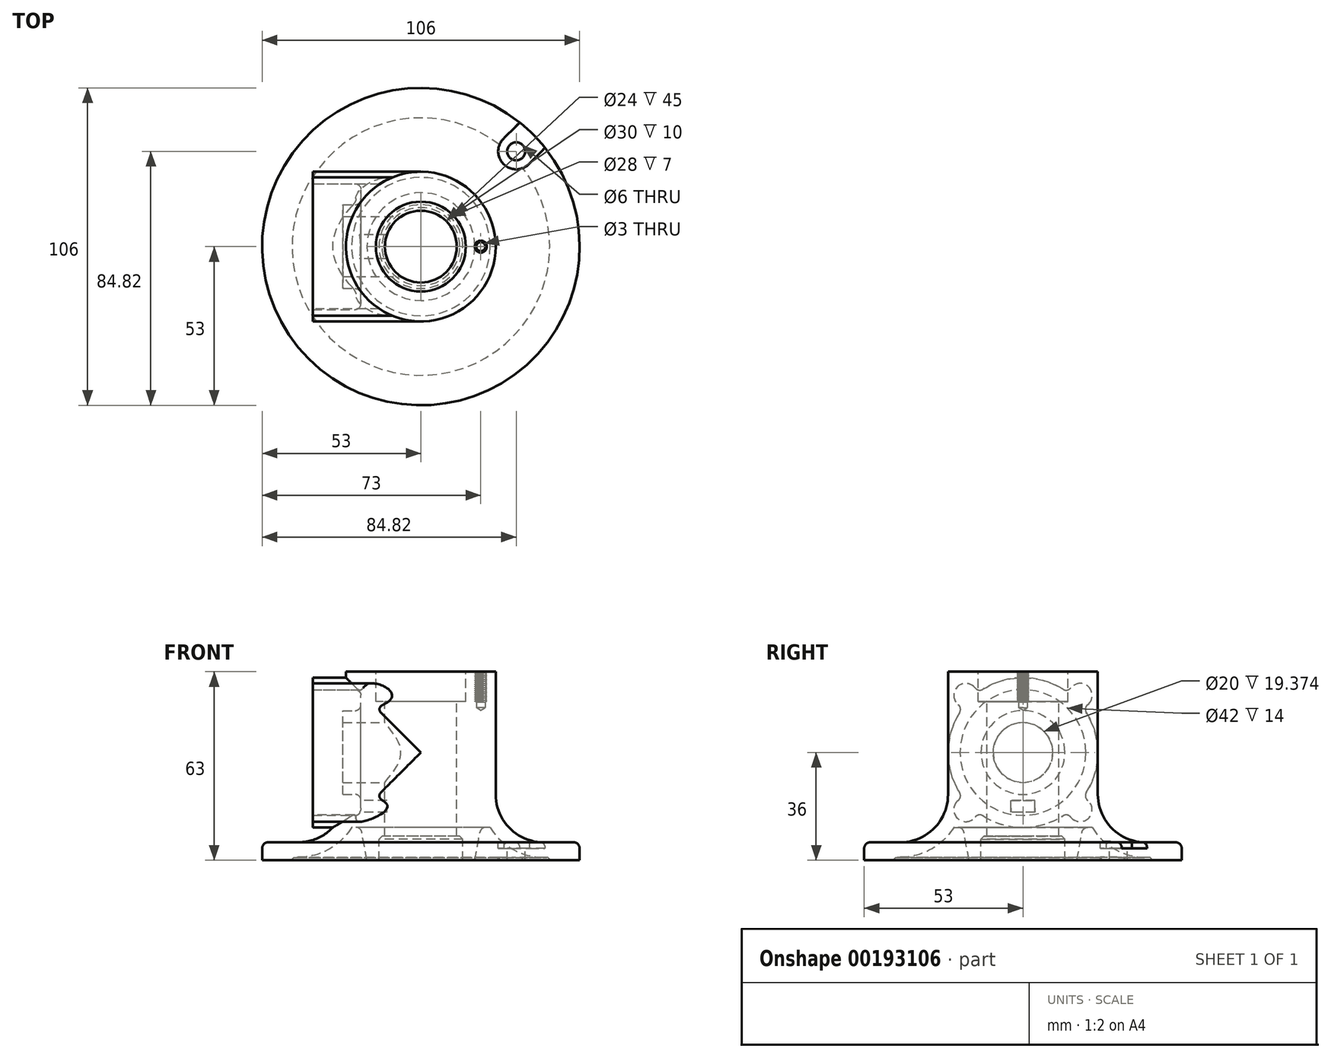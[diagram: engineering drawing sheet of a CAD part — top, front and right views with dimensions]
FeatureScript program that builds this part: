
annotation { "Feature Type Name" : "Feature", "Feature Type Description" : "" }
export const myFeature = defineFeature(function(context is Context, id is Id, definition is map)
    precondition{}
    {
        {
            var Q0;
            Q0=qCreatedBy(makeId("Top.planeOp"),FACE);
            var sketch = newSketch(context, id + "F0", { "sketchPlane" : qUnion([Q0])});
            skCircle(sketch, "E0", {"center": v(0, 0) * mm, "radius": 53 * mm});
            skCircle(sketch, "E1", {"center": v(0, 0) * mm, "radius": 25 * mm});
            skSolve(sketch);
        }
        {
            var Q0;
            Q0 = qSketchRegion(id + "F0", true);
            var Q1;
            Q1=makeQuery(id+"F0.imprint","IMPRINT",FACE,{"disambiguationData":[TD([[makeQuery(id+"F0.imprint","IMPRINT",EDGE,{"derivedFrom":sQuery(id+"F0.wireOp",EDGE,"E1")}),1.0]])]});
            extrude(context, id + "F1", {"entities" : qUnion([Q0, Q1]), "depth" : 6 * mm});
        }
        {
            var Q0;
            Q0=makeQuery(id+"F0.imprint","IMPRINT",FACE,{"disambiguationData":[TD([[makeQuery(id+"F0.imprint","IMPRINT",EDGE,{"derivedFrom":sQuery(id+"F0.wireOp",EDGE,"E1")}),1.0]])]});
            extrude(context, id + "F2", {"entities" : qUnion([Q0]), "operationType" : NewBodyOperationType.ADD, "depth" : 63 * mm});
        }
        {
            var Q0;
            Q0=makeQuery(id+"F2.boolean.opBoolean","INTERSECT",EDGE,{"derivedFrom":[makeQuery(id+"F1.opExtrude","CAP_FACE",FACE,{"disambiguationData":[OSD([sQuery(id+"F0.wireOp",EDGE,"E0")])],"isStart":false}),makeQuery(id+"F2.opExtrude","SWEPT_FACE",FACE,{"disambiguationData":[OSD([sQuery(id+"F0.wireOp",EDGE,"E1")])]})]});
            fillet(context, id + "F3", {"entities" : qUnion([Q0]), "radius" : 16 * mm, "tangentPropagation" : true, "allowEdgeOverflow" : false});
        }
        {
            var Q0;
            Q0=makeQuery(id+"F1.opExtrude","CAP_EDGE",EDGE,{"disambiguationData":[OSD([sQuery(id+"F0.wireOp",EDGE,"E0")])],"isStart":false});
            fillet(context, id + "F4", {"entities" : qUnion([Q0]), "radius" : 2 * mm, "tangentPropagation" : true, "allowEdgeOverflow" : false});
        }
        {
            var Q0;
            Q0=qCreatedBy(makeId("Front.planeOp"),FACE);
            var sketch = newSketch(context, id + "F5", { "sketchPlane" : qUnion([Q0])});
            skLineSegment(sketch, "E2", {"start": v(0, 0) * mm, "end": v(0, 69) * mm, "construction": true});
            skLineSegment(sketch, "E3.0", {"start": v(0, 63) * mm, "end": v(25, 63) * mm});
            skLineSegment(sketch, "E4", {"start": v(15, 63) * mm, "end": v(15, 53) * mm});
            skLineSegment(sketch, "E5", {"start": v(15, 53) * mm, "end": v(12, 53) * mm});
            skLineSegment(sketch, "E6", {"start": v(12, 53) * mm, "end": v(12, 8) * mm});
            skLineSegment(sketch, "E7", {"start": v(12, 8) * mm, "end": v(14, 8) * mm});
            skLineSegment(sketch, "E8", {"start": v(14, 8) * mm, "end": v(14, 0) * mm});
            skLineSegment(sketch, "E9", {"start": v(14, 0) * mm, "end": v(0, 0) * mm});
            skLineSegment(sketch, "E10", {"start": v(0, 63) * mm, "end": v(0, 0) * mm});
            skPoint(sketch, "E11.orphan", {"position": v(-25, 63) * mm});
            skArc(sketch, "E12", {"start": v(25, 22) * mm, "mid": v(29.69, 10.69) * mm, "end": v(41, 6) * mm});
            skArc(sketch, "E13.0", {"start": v(23.11, 11) * mm, "mid": v(30.75, 3.67) * mm, "end": v(41, 1) * mm});
            skLineSegment(sketch, "E14.0", {"start": v(-53, 0) * mm, "end": v(14, 0) * mm});
            skLineSegment(sketch, "E15", {"start": v(18, 0) * mm, "end": v(20, 11) * mm});
            skLineSegment(sketch, "E16", {"start": v(20, 11) * mm, "end": v(23.11, 11) * mm});
            skLineSegment(sketch, "E17", {"start": v(43, 0) * mm, "end": v(43, 0) * mm});
            skLineSegment(sketch, "E18.trimOffspring", {"start": v(18, 0) * mm, "end": v(43, 0) * mm});
            skPoint(sketch, "E19.orphan", {"position": v(53, 0) * mm});
            skLineSegment(sketch, "E20", {"start": v(41, 1) * mm, "end": v(42, 1) * mm});
            skPoint(sketch, "E21.visualSharp", {"position": v(43, 1) * mm});
            skArc(sketch, "E21.filletArc", {"start": v(43, 0) * mm, "mid": v(42.7, 0.7) * mm, "end": v(42, 1) * mm});
            skSolve(sketch);
        }
        {
            var Q0;
            Q0 = qSketchRegion(id + "F5", true);
            var Q1;
            Q1=sQuery(id+"F5.wireOp",EDGE,"E2");
            revolve(context, id + "F6", {"operationType" : NewBodyOperationType.REMOVE, "entities" : qUnion([Q0]), "axis" : qUnion([Q1]), "revolveType" : RevolveType.FULL, "oppositeDirection" : true});
        }
        {
            var Q0;
            Q0=qCreatedBy(makeId("Right.planeOp"),FACE);
            cPlane(context, id + "F7", {"entities" : qUnion([Q0]), "cplaneType" : CPlaneType.OFFSET, "offset" : 36 * mm, "oppositeDirection" : true, "width" : 150 * mm, "height" : 150 * mm});
        }
        {
            var Q0;
            Q0=qCreatedBy(id+"F7.planeOp",FACE);
            var sketch = newSketch(context, id + "F8", { "sketchPlane" : qUnion([Q0])});
            skArc(sketch, "E22", {"start": v(-21.15, 49.34) * mm, "mid": v(-25, 36) * mm, "end": v(-21.15, 22.66) * mm});
            skLineSegment(sketch, "E23", {"start": v(-25, 22) * mm, "end": v(-25, 63) * mm});
            skCircle(sketch, "E24", {"center": v(0, 36) * mm, "radius": 27 * mm, "construction": true});
            skLineSegment(sketch, "E25", {"start": v(0, 36) * mm, "end": v(-36.16, 36) * mm, "construction": true});
            skLineSegment(sketch, "E26", {"start": v(0, 36) * mm, "end": v(-20.86, 56.86) * mm, "construction": true});
            skArc(sketch, "E27", {"start": v(-15.97, 57.59) * mm, "mid": v(-21.92, 57.92) * mm, "end": v(-21.59, 51.97) * mm});
            skPoint(sketch, "E28.visualSharp", {"position": v(-15.17, 55.87) * mm});
            skArc(sketch, "E28.filletArc", {"start": v(-15.97, 57.59) * mm, "mid": v(-14.74, 56.86) * mm, "end": v(-13.34, 57.15) * mm});
            skPoint(sketch, "E29.visualSharp", {"position": v(-19.87, 51.17) * mm});
            skArc(sketch, "E29.filletArc", {"start": v(-21.15, 49.34) * mm, "mid": v(-20.86, 50.74) * mm, "end": v(-21.59, 51.97) * mm});
            skArc(sketch, "E30.1.0", {"start": v(-21.59, 20.03) * mm, "mid": v(-20.86, 21.26) * mm, "end": v(-21.15, 22.66) * mm});
            skArc(sketch, "E30.1.1", {"start": v(-21.59, 20.03) * mm, "mid": v(-21.92, 14.08) * mm, "end": v(-15.97, 14.41) * mm});
            skArc(sketch, "E30.1.2", {"start": v(-13.34, 14.85) * mm, "mid": v(-14.74, 15.14) * mm, "end": v(-15.97, 14.41) * mm});
            skArc(sketch, "E30.2.0", {"start": v(15.97, 14.41) * mm, "mid": v(14.74, 15.14) * mm, "end": v(13.34, 14.85) * mm});
            skArc(sketch, "E30.2.1", {"start": v(15.97, 14.41) * mm, "mid": v(21.92, 14.08) * mm, "end": v(21.59, 20.03) * mm});
            skArc(sketch, "E30.2.2", {"start": v(21.15, 22.66) * mm, "mid": v(20.86, 21.26) * mm, "end": v(21.59, 20.03) * mm});
            skArc(sketch, "E30.3.0", {"start": v(21.59, 51.97) * mm, "mid": v(20.86, 50.74) * mm, "end": v(21.15, 49.34) * mm});
            skArc(sketch, "E30.3.1", {"start": v(21.59, 51.97) * mm, "mid": v(21.92, 57.92) * mm, "end": v(15.97, 57.59) * mm});
            skArc(sketch, "E30.3.2", {"start": v(13.34, 57.15) * mm, "mid": v(14.74, 56.86) * mm, "end": v(15.97, 57.59) * mm});
            skArc(sketch, "E31.trimOffspring", {"start": v(13.34, 57.15) * mm, "mid": v(0, 61) * mm, "end": v(-13.34, 57.15) * mm});
            skArc(sketch, "E32.trimOffspring", {"start": v(21.15, 22.66) * mm, "mid": v(25, 36) * mm, "end": v(21.15, 49.34) * mm});
            skArc(sketch, "E33.trimOffspring", {"start": v(-13.34, 14.85) * mm, "mid": v(0, 11) * mm, "end": v(13.34, 14.85) * mm});
            skSolve(sketch);
        }
        {
            var Q0;
            Q0 = qSketchRegion(id + "F8", true);
            extrude(context, id + "F9", {"entities" : qUnion([Q0]), "operationType" : NewBodyOperationType.ADD, "endBound" : BoundingType.UP_TO_NEXT, "depth" : 25 * mm});
        }
        {
            var Q0;
            Q0=qCreatedBy(makeId("Front.planeOp"),FACE);
            var sketch = newSketch(context, id + "F10", { "sketchPlane" : qUnion([Q0])});
            skLineSegment(sketch, "E34.0", {"start": v(-36, 49.34) * mm, "end": v(-36, 36) * mm});
            skLineSegment(sketch, "E35", {"start": v(-36, 36) * mm, "end": v(22.04, 36) * mm, "construction": true});
            skLineSegment(sketch, "E36.0", {"start": v(-36, 49.34) * mm, "end": v(-36, 51.97) * mm});
            skLineSegment(sketch, "E37.0", {"start": v(-36, 57) * mm, "end": v(-36, 51.97) * mm});
            skLineSegment(sketch, "E38", {"start": v(-36, 57) * mm, "end": v(-22, 57) * mm});
            skLineSegment(sketch, "E39", {"start": v(-20, 55) * mm, "end": v(-20, 52) * mm});
            skLineSegment(sketch, "E40", {"start": v(-22, 50) * mm, "end": v(-26, 50) * mm});
            skLineSegment(sketch, "E41", {"start": v(-26, 50) * mm, "end": v(-26, 46) * mm});
            skLineSegment(sketch, "E42", {"start": v(-26, 46) * mm, "end": v(0, 46) * mm});
            skLineSegment(sketch, "E43", {"start": v(0, 46) * mm, "end": v(0, 36) * mm});
            skLineSegment(sketch, "E44", {"start": v(0, 36) * mm, "end": v(-36, 36) * mm});
            skPoint(sketch, "E45.orphan", {"position": v(-36, 59.1) * mm});
            skPoint(sketch, "E46.orphan", {"position": v(-36, 22.66) * mm});
            skPoint(sketch, "E47.visualSharp", {"position": v(-20, 57) * mm});
            skArc(sketch, "E47.filletArc", {"start": v(-20, 55) * mm, "mid": v(-20.59, 56.41) * mm, "end": v(-22, 57) * mm});
            skPoint(sketch, "E48.visualSharp", {"position": v(-20, 50) * mm});
            skArc(sketch, "E48.filletArc", {"start": v(-22, 50) * mm, "mid": v(-20.59, 50.59) * mm, "end": v(-20, 52) * mm});
            skSolve(sketch);
        }
        {
            var Q0;
            Q0 = qSketchRegion(id + "F10", true);
            var Q1;
            Q1=sQuery(id+"F10.wireOp",EDGE,"E35");
            revolve(context, id + "F11", {"operationType" : NewBodyOperationType.REMOVE, "entities" : qUnion([Q0]), "axis" : qUnion([Q1]), "revolveType" : RevolveType.FULL, "oppositeDirection" : true});
        }
        {
            var Q0;
            Q0=makeQuery(id+"F11.boolean.opBoolean","COPY",FACE,{"derivedFrom":makeQuery(id+"F11.opRevolve","SWEPT_FACE",FACE,{"disambiguationData":[OSD([sQuery(id+"F10.wireOp",EDGE,"E39")])]})});
            var sketch = newSketch(context, id + "F12", { "sketchPlane" : qUnion([Q0])});
            skLineSegment(sketch, "E49", {"start": v(0, 0) * mm, "end": v(0, 36) * mm, "construction": true});
            skLineSegment(sketch, "E50.bottom", {"start": v(4, 16) * mm, "end": v(-4, 16) * mm});
            skLineSegment(sketch, "E50.top", {"start": v(4, 20) * mm, "end": v(-4, 20) * mm});
            skLineSegment(sketch, "E50.left", {"start": v(4, 16) * mm, "end": v(4, 20) * mm});
            skLineSegment(sketch, "E50.right", {"start": v(-4, 16) * mm, "end": v(-4, 20) * mm});
            skPoint(sketch, "E50.middle", {"position": v(0, 18) * mm});
            skSolve(sketch);
        }
        {
            var Q0;
            Q0 = qSketchRegion(id + "F12", true);
            var Q1;
            Q1=makeQuery(id+"F9.opExtrude","CAP_FACE",FACE,{"disambiguationData":[OSD([sQuery(id+"F8.wireOp",EDGE,"E22"),sQuery(id+"F8.wireOp",EDGE,"E27"),sQuery(id+"F8.wireOp",EDGE,"E28.filletArc"),sQuery(id+"F8.wireOp",EDGE,"E29.filletArc"),sQuery(id+"F8.wireOp",EDGE,"E30.1.0"),sQuery(id+"F8.wireOp",EDGE,"E30.1.1"),sQuery(id+"F8.wireOp",EDGE,"E30.1.2"),sQuery(id+"F8.wireOp",EDGE,"E30.2.0"),sQuery(id+"F8.wireOp",EDGE,"E30.2.1"),sQuery(id+"F8.wireOp",EDGE,"E30.2.2"),sQuery(id+"F8.wireOp",EDGE,"E30.3.0"),sQuery(id+"F8.wireOp",EDGE,"E30.3.1"),sQuery(id+"F8.wireOp",EDGE,"E30.3.2"),sQuery(id+"F8.wireOp",EDGE,"E31.trimOffspring"),sQuery(id+"F8.wireOp",EDGE,"E32.trimOffspring"),sQuery(id+"F8.wireOp",EDGE,"E33.trimOffspring")])],"isStart":true});
            extrude(context, id + "F13", {"entities" : qUnion([Q0]), "operationType" : NewBodyOperationType.REMOVE, "endBound" : BoundingType.UP_TO_NEXT, "oppositeDirection" : true, "depth" : 25 * mm, "hasSecondDirection" : true, "secondDirectionBound" : BoundingType.UP_TO_SURFACE, "secondDirectionOppositeDirection" : false, "secondDirectionBoundEntityFace" : qUnion([Q1]), "secondDirectionDepth" : 25 * mm});
        }
        {
            var Q0;
            Q0=makeQuery(id+"F1.opExtrude","CAP_FACE",FACE,{"disambiguationData":[OSD([sQuery(id+"F0.wireOp",EDGE,"E0")])],"isStart":false});
            var sketch = newSketch(context, id + "F14", { "sketchPlane" : qUnion([Q0])});
            skCircle(sketch, "E51", {"center": v(0, 0) * mm, "radius": 45 * mm, "construction": true});
            skLineSegment(sketch, "E52", {"start": v(0, 0) * mm, "end": v(65.75, 0) * mm, "construction": true});
            skLineSegment(sketch, "E53", {"start": v(0, 0) * mm, "end": v(45.32, 45.32) * mm, "construction": true});
            skArc(sketch, "E54", {"start": v(27.87, 36.34) * mm, "mid": v(27.58, 27.58) * mm, "end": v(36.34, 27.87) * mm});
            skLineSegment(sketch, "E55", {"start": v(27.3, 35.77) * mm, "end": v(33, 41.47) * mm});
            skLineSegment(sketch, "E56.MirrorCS", {"start": v(35.77, 27.3) * mm, "end": v(41.47, 33) * mm});
            skArc(sketch, "E57.0", {"start": v(41.47, 33) * mm, "mid": v(37.48, 37.48) * mm, "end": v(33, 41.47) * mm});
            skPoint(sketch, "E58.orphan", {"position": v(33.39, 41.86) * mm});
            skPoint(sketch, "E59.orphan", {"position": v(41.86, 33.39) * mm});
            skCircle(sketch, "E60", {"center": v(31.82, 31.82) * mm, "radius": 3 * mm});
            skSolve(sketch);
        }
        {
            var Q0;
            Q0 = qSketchRegion(id + "F14", true);
            var Q1;
            Q1=makeQuery(id+"F14.imprint","IMPRINT",FACE,{"disambiguationData":[TD([[makeQuery(id+"F14.imprint","IMPRINT",EDGE,{"derivedFrom":sQuery(id+"F14.wireOp",EDGE,"E60")}),1.0]])]});
            extrude(context, id + "F15", {"entities" : qUnion([Q0, Q1]), "operationType" : NewBodyOperationType.REMOVE, "oppositeDirection" : true, "depth" : 2 * mm, "hasSecondDirection" : true, "secondDirectionOppositeDirection" : false, "secondDirectionDepth" : 2 * mm});
        }
        {
            var Q0;
            Q0=makeQuery(id+"F15.boolean.opBoolean","COPY",FACE,{"derivedFrom":makeQuery(id+"F15.opExtrude","CAP_FACE",FACE,{"disambiguationData":[OSD([sQuery(id+"F14.wireOp",EDGE,"E54"),sQuery(id+"F14.wireOp",EDGE,"E55"),sQuery(id+"F14.wireOp",EDGE,"E56.MirrorCS"),sQuery(id+"F14.wireOp",EDGE,"E57.0")])],"isStart":false})});
            var sketch = newSketch(context, id + "F16", { "sketchPlane" : qUnion([Q0])});
            skArc(sketch, "E61.0.0", {"start": v(27.87, 36.34) * mm, "mid": v(27.58, 27.58) * mm, "end": v(36.34, 27.87) * mm});
            skLineSegment(sketch, "E61.0.1", {"start": v(36.34, 27.87) * mm, "end": v(41.47, 33) * mm});
            skArc(sketch, "E61.0.2", {"start": v(33, 41.47) * mm, "mid": v(37.48, 37.48) * mm, "end": v(41.47, 33) * mm});
            skLineSegment(sketch, "E61.0.3", {"start": v(33, 41.47) * mm, "end": v(27.87, 36.34) * mm});
            skSolve(sketch);
        }
        {
            var Q0;
            Q0 = qSketchRegion(id + "F16", true);
            var Q1;
            {var subQ0=sQuery(id+"F0.wireOp",EDGE,"E0");Q1=makeQuery(id+"F6.boolean.opBoolean","SPLIT",FACE,{"disambiguationData":[TD([makeQuery(id+"F1.opExtrude","SWEPT_FACE",FACE,{"disambiguationData":[OSD([subQ0])]})])],"derivedFrom":makeQuery(id+"F1.opExtrude","CAP_FACE",FACE,{"disambiguationData":[OSD([subQ0])],"isStart":true})});}
            extrude(context, id + "F17", {"entities" : qUnion([Q0]), "operationType" : NewBodyOperationType.ADD, "endBound" : BoundingType.UP_TO_SURFACE, "oppositeDirection" : true, "endBoundEntityFace" : qUnion([Q1]), "depth" : 25 * mm});
        }
        {
            var Q0;
            Q0=makeQuery(id+"F14.imprint","IMPRINT",FACE,{"disambiguationData":[TD([[makeQuery(id+"F14.imprint","IMPRINT",EDGE,{"derivedFrom":sQuery(id+"F14.wireOp",EDGE,"E60")}),1.0]])]});
            extrude(context, id + "F18", {"entities" : qUnion([Q0]), "operationType" : NewBodyOperationType.REMOVE, "endBound" : BoundingType.THROUGH_ALL, "oppositeDirection" : true, "depth" : 25 * mm});
        }
        {
            var Q0;
            Q0=qCreatedBy(makeId("Front.planeOp"),FACE);
            var sketch = newSketch(context, id + "F19", { "sketchPlane" : qUnion([Q0])});
            skLineSegment(sketch, "E62", {"start": v(20, 78.44) * mm, "end": v(20, 37.25) * mm, "construction": true});
            skLineSegment(sketch, "E63.0", {"start": v(-25, 63) * mm, "end": v(22, 63) * mm});
            skLineSegment(sketch, "E64", {"start": v(22, 63) * mm, "end": v(21.5, 62.65) * mm});
            skLineSegment(sketch, "E65", {"start": v(21.5, 62.65) * mm, "end": v(22, 62.3) * mm});
            skLineSegment(sketch, "E66.1.0.0", {"start": v(22, 62.3) * mm, "end": v(21.5, 61.95) * mm});
            skLineSegment(sketch, "E66.1.0.1", {"start": v(21.5, 61.95) * mm, "end": v(22, 61.6) * mm});
            skLineSegment(sketch, "E66.2.0.0", {"start": v(22, 61.6) * mm, "end": v(21.5, 61.25) * mm});
            skLineSegment(sketch, "E66.2.0.1", {"start": v(21.5, 61.25) * mm, "end": v(22, 60.9) * mm});
            skLineSegment(sketch, "E66.3.0.0", {"start": v(22, 60.9) * mm, "end": v(21.5, 60.55) * mm});
            skLineSegment(sketch, "E66.3.0.1", {"start": v(21.5, 60.55) * mm, "end": v(22, 60.2) * mm});
            skLineSegment(sketch, "E66.4.0.0", {"start": v(22, 60.2) * mm, "end": v(21.5, 59.85) * mm});
            skLineSegment(sketch, "E66.4.0.1", {"start": v(21.5, 59.85) * mm, "end": v(22, 59.5) * mm});
            skLineSegment(sketch, "E66.5.0.0", {"start": v(22, 59.5) * mm, "end": v(21.5, 59.15) * mm});
            skLineSegment(sketch, "E66.5.0.1", {"start": v(21.5, 59.15) * mm, "end": v(22, 58.8) * mm});
            skLineSegment(sketch, "E66.6.0.0", {"start": v(22, 58.8) * mm, "end": v(21.5, 58.45) * mm});
            skLineSegment(sketch, "E66.6.0.1", {"start": v(21.5, 58.45) * mm, "end": v(22, 58.1) * mm});
            skLineSegment(sketch, "E66.7.0.0", {"start": v(22, 58.1) * mm, "end": v(21.5, 57.75) * mm});
            skLineSegment(sketch, "E66.7.0.1", {"start": v(21.5, 57.75) * mm, "end": v(22, 57.4) * mm});
            skLineSegment(sketch, "E66.8.0.0", {"start": v(22, 57.4) * mm, "end": v(21.5, 57.05) * mm});
            skLineSegment(sketch, "E66.8.0.1", {"start": v(21.5, 57.05) * mm, "end": v(22, 56.7) * mm});
            skLineSegment(sketch, "E66.9.0.0", {"start": v(22, 56.7) * mm, "end": v(21.5, 56.35) * mm});
            skLineSegment(sketch, "E66.9.0.1", {"start": v(21.5, 56.35) * mm, "end": v(22, 56) * mm});
            skLineSegment(sketch, "E66.10.0.0", {"start": v(22, 56) * mm, "end": v(21.5, 55.65) * mm});
            skLineSegment(sketch, "E66.10.0.1", {"start": v(21.5, 55.65) * mm, "end": v(22, 55.3) * mm});
            skLineSegment(sketch, "E66.11.0.0", {"start": v(22, 55.3) * mm, "end": v(21.5, 54.95) * mm});
            skLineSegment(sketch, "E66.11.0.1", {"start": v(21.5, 54.95) * mm, "end": v(22, 54.6) * mm});
            skLineSegment(sketch, "E66.12.0.0", {"start": v(22, 54.6) * mm, "end": v(21.5, 54.25) * mm});
            skLineSegment(sketch, "E66.12.0.1", {"start": v(21.5, 54.25) * mm, "end": v(22, 53.9) * mm});
            skLineSegment(sketch, "E66.13.0.0", {"start": v(22, 53.9) * mm, "end": v(21.5, 53.55) * mm});
            skLineSegment(sketch, "E66.13.0.1", {"start": v(21.5, 53.55) * mm, "end": v(22, 53.2) * mm});
            skLineSegment(sketch, "E66.14.0.0", {"start": v(22, 53.2) * mm, "end": v(21.5, 52.85) * mm});
            skLineSegment(sketch, "E66.direction1", {"start": v(21.5, 62.65) * mm, "end": v(21.5, 61.95) * mm, "construction": true});
            skLineSegment(sketch, "E67", {"start": v(21.5, 52.85) * mm, "end": v(21.5, 51) * mm});
            skLineSegment(sketch, "E68", {"start": v(21.5, 51) * mm, "end": v(20, 50.1) * mm});
            skLineSegment(sketch, "E69", {"start": v(20, 50.1) * mm, "end": v(20, 63) * mm});
            skLineSegment(sketch, "E70", {"start": v(20, 63) * mm, "end": v(22, 63) * mm});
            skPoint(sketch, "E71.orphan", {"position": v(25, 63) * mm});
            skSolve(sketch);
        }
        {
            var Q0;
            Q0 = qSketchRegion(id + "F19", true);
            var Q1;
            Q1=sQuery(id+"F19.wireOp",EDGE,"E62");
            revolve(context, id + "F20", {"operationType" : NewBodyOperationType.REMOVE, "entities" : qUnion([Q0]), "axis" : qUnion([Q1]), "revolveType" : RevolveType.FULL, "oppositeDirection" : true});
        }
        {
            var Q0;
            Q0=makeQuery(id+"F11.boolean.opBoolean","COPY",FACE,{"derivedFrom":makeQuery(id+"F11.opRevolve","SWEPT_FACE",FACE,{"disambiguationData":[OSD([sQuery(id+"F10.wireOp",EDGE,"E38")])]})});
            cPlane(context, id + "F21", {"entities" : qUnion([Q0]), "cplaneType" : CPlaneType.LINE_ANGLE, "offset" : 25 * mm, "angle" : 135 * degree, "width" : 150 * mm, "height" : 150 * mm});
        }
        {
            var Q0;
            Q0=qCreatedBy(id+"F21.planeOp",FACE);
            var sketch = newSketch(context, id + "F22", { "sketchPlane" : qUnion([Q0])});
            skLineSegment(sketch, "E72", {"start": v(-43.3, -52.46) * mm, "end": v(-4.44, -52.46) * mm, "construction": true});
            skLineSegment(sketch, "E73.0", {"start": v(-36, -52.01) * mm, "end": v(-36, -54.46) * mm});
            skLineSegment(sketch, "E74", {"start": v(-36, -54.46) * mm, "end": v(-35.65, -53.96) * mm});
            skLineSegment(sketch, "E75", {"start": v(-35.65, -53.96) * mm, "end": v(-35.3, -54.46) * mm});
            skLineSegment(sketch, "E76.1.0.0", {"start": v(-35.3, -54.46) * mm, "end": v(-34.95, -53.96) * mm});
            skLineSegment(sketch, "E76.1.0.1", {"start": v(-34.95, -53.96) * mm, "end": v(-34.6, -54.46) * mm});
            skLineSegment(sketch, "E76.2.0.0", {"start": v(-34.6, -54.46) * mm, "end": v(-34.25, -53.96) * mm});
            skLineSegment(sketch, "E76.2.0.1", {"start": v(-34.25, -53.96) * mm, "end": v(-33.9, -54.46) * mm});
            skLineSegment(sketch, "E76.3.0.0", {"start": v(-33.9, -54.46) * mm, "end": v(-33.55, -53.96) * mm});
            skLineSegment(sketch, "E76.3.0.1", {"start": v(-33.55, -53.96) * mm, "end": v(-33.2, -54.46) * mm});
            skLineSegment(sketch, "E76.4.0.0", {"start": v(-33.2, -54.46) * mm, "end": v(-32.85, -53.96) * mm});
            skLineSegment(sketch, "E76.4.0.1", {"start": v(-32.85, -53.96) * mm, "end": v(-32.5, -54.46) * mm});
            skLineSegment(sketch, "E76.5.0.0", {"start": v(-32.5, -54.46) * mm, "end": v(-32.15, -53.96) * mm});
            skLineSegment(sketch, "E76.5.0.1", {"start": v(-32.15, -53.96) * mm, "end": v(-31.8, -54.46) * mm});
            skLineSegment(sketch, "E76.6.0.0", {"start": v(-31.8, -54.46) * mm, "end": v(-31.45, -53.96) * mm});
            skLineSegment(sketch, "E76.6.0.1", {"start": v(-31.45, -53.96) * mm, "end": v(-31.1, -54.46) * mm});
            skLineSegment(sketch, "E76.7.0.0", {"start": v(-31.1, -54.46) * mm, "end": v(-30.75, -53.96) * mm});
            skLineSegment(sketch, "E76.7.0.1", {"start": v(-30.75, -53.96) * mm, "end": v(-30.4, -54.46) * mm});
            skLineSegment(sketch, "E76.8.0.0", {"start": v(-30.4, -54.46) * mm, "end": v(-30.05, -53.96) * mm});
            skLineSegment(sketch, "E76.8.0.1", {"start": v(-30.05, -53.96) * mm, "end": v(-29.7, -54.46) * mm});
            skLineSegment(sketch, "E76.9.0.0", {"start": v(-29.7, -54.46) * mm, "end": v(-29.35, -53.96) * mm});
            skLineSegment(sketch, "E76.9.0.1", {"start": v(-29.35, -53.96) * mm, "end": v(-29, -54.46) * mm});
            skLineSegment(sketch, "E76.10.0.0", {"start": v(-29, -54.46) * mm, "end": v(-28.65, -53.96) * mm});
            skLineSegment(sketch, "E76.10.0.1", {"start": v(-28.65, -53.96) * mm, "end": v(-28.3, -54.46) * mm});
            skLineSegment(sketch, "E76.11.0.0", {"start": v(-28.3, -54.46) * mm, "end": v(-27.95, -53.96) * mm});
            skLineSegment(sketch, "E76.11.0.1", {"start": v(-27.95, -53.96) * mm, "end": v(-27.6, -54.46) * mm});
            skLineSegment(sketch, "E76.12.0.0", {"start": v(-27.6, -54.46) * mm, "end": v(-27.25, -53.96) * mm});
            skLineSegment(sketch, "E76.12.0.1", {"start": v(-27.25, -53.96) * mm, "end": v(-26.9, -54.46) * mm});
            skLineSegment(sketch, "E76.13.0.0", {"start": v(-26.9, -54.46) * mm, "end": v(-26.55, -53.96) * mm});
            skLineSegment(sketch, "E76.13.0.1", {"start": v(-26.55, -53.96) * mm, "end": v(-26.2, -54.46) * mm});
            skLineSegment(sketch, "E76.14.0.0", {"start": v(-26.2, -54.46) * mm, "end": v(-25.85, -53.96) * mm});
            skLineSegment(sketch, "E76.direction1", {"start": v(-36, -54.46) * mm, "end": v(-35.3, -54.46) * mm, "construction": true});
            skLineSegment(sketch, "E77", {"start": v(-25.85, -53.96) * mm, "end": v(-24, -53.96) * mm});
            skLineSegment(sketch, "E78", {"start": v(-24, -53.96) * mm, "end": v(-23.1, -52.46) * mm});
            skLineSegment(sketch, "E79", {"start": v(-23.1, -52.46) * mm, "end": v(-36, -52.46) * mm});
            skPoint(sketch, "E80.orphan", {"position": v(-36, -56.46) * mm});
            skSolve(sketch);
        }
        {
            var Q0;
            Q0 = qSketchRegion(id + "F22", true);
            var Q1;
            Q1=sQuery(id+"F22.wireOp",EDGE,"E72");
            revolve(context, id + "F23", {"operationType" : NewBodyOperationType.REMOVE, "entities" : qUnion([Q0]), "axis" : qUnion([Q1]), "revolveType" : RevolveType.FULL, "oppositeDirection" : true});
        }
        {
            var Q0;
            Q0=makeQuery(id+"F6.boolean.opBoolean","COPY",EDGE,{"derivedFrom":makeQuery(id+"F6.opRevolve","SWEPT_EDGE",EDGE,{"disambiguationData":[OSD([sQuery(id+"F5.wireOp",EDGE,"E3.0"),sQuery(id+"F5.wireOp",EDGE,"E4")])]})});
            var Q1;
            Q1=makeQuery(id+"F6.boolean.opBoolean","COPY",EDGE,{"derivedFrom":makeQuery(id+"F6.opRevolve","SWEPT_EDGE",EDGE,{"disambiguationData":[OSD([sQuery(id+"F5.wireOp",EDGE,"E8"),sQuery(id+"F5.wireOp",EDGE,"E14.0")])]})});
            var Q2;
            Q2=makeQuery(id+"F11.boolean.opBoolean","COPY",EDGE,{"derivedFrom":makeQuery(id+"F11.opRevolve","SWEPT_EDGE",EDGE,{"disambiguationData":[OSD([sQuery(id+"F10.wireOp",EDGE,"E37.0"),sQuery(id+"F10.wireOp",EDGE,"E38")])]})});
            chamfer(context, id + "F24", {"entities" : qUnion([Q0, Q1, Q2]), "width" : 1 * mm, "tangentPropagation" : true});
        }
        {
            var Q0;
            Q0=makeQuery(id+"F9.opExtrude","CAP_EDGE",EDGE,{"disambiguationData":[OSD([sQuery(id+"F8.wireOp",EDGE,"E31.trimOffspring")])],"isStart":false});
            var Q1;
            Q1=makeQuery(id+"F9.opExtrude","CAP_EDGE",EDGE,{"disambiguationData":[OSD([sQuery(id+"F8.wireOp",EDGE,"E22")]),OD(1.0)],"isStart":false});
            var Q2;
            {var subQ0=sQuery(id+"F12.wireOp",EDGE,"E50.right");var subQ2=sQuery(id+"F12.wireOp",EDGE,"E50.bottom");Q2=makeQuery(id+"F13.boolean.opBoolean","COPY",EDGE,{"derivedFrom":makeQuery(id+"F13.opExtrude","TWEAK_EDGE",EDGE,{"derivedFrom":[makeQuery(id+"F12.imprint","IMPRINT",EDGE,{"derivedFrom":subQ2}),makeQuery(id+"F12.imprint","IMPRINT",EDGE,{"disambiguationData":[TD([[makeQuery(id+"F12.imprint","INTERSECT",VERTEX,{"derivedFrom":[subQ2,subQ0]}),-1.0]])],"derivedFrom":subQ0}),makeQuery(id+"F12.imprint","IMPRINT",EDGE,{"disambiguationData":[TD([[makeQuery(id+"F12.imprint","INTERSECT",VERTEX,{"derivedFrom":[sQuery(id+"F12.wireOp",EDGE,"E50.top"),subQ0]}),1.0]])],"derivedFrom":subQ0})]})});}
            var Q3;
            {var subQ0=sQuery(id+"F12.wireOp",EDGE,"E50.left");var subQ2=sQuery(id+"F12.wireOp",EDGE,"E50.bottom");Q3=makeQuery(id+"F13.boolean.opBoolean","COPY",EDGE,{"derivedFrom":makeQuery(id+"F13.opExtrude","TWEAK_EDGE",EDGE,{"derivedFrom":[makeQuery(id+"F12.imprint","IMPRINT",EDGE,{"derivedFrom":subQ2}),makeQuery(id+"F12.imprint","IMPRINT",EDGE,{"disambiguationData":[TD([[makeQuery(id+"F12.imprint","INTERSECT",VERTEX,{"derivedFrom":[subQ2,subQ0]}),-1.0]])],"derivedFrom":subQ0}),makeQuery(id+"F12.imprint","IMPRINT",EDGE,{"disambiguationData":[TD([[makeQuery(id+"F12.imprint","INTERSECT",VERTEX,{"derivedFrom":[sQuery(id+"F12.wireOp",EDGE,"E50.top"),subQ0]}),1.0]])],"derivedFrom":subQ0})]})});}
            var Q4;
            {var subQ0=sQuery(id+"F12.wireOp",EDGE,"E50.left");var subQ1=sQuery(id+"F12.wireOp",EDGE,"E50.top");var subQ2=makeQuery(id+"F12.imprint","INTERSECT",VERTEX,{"derivedFrom":[subQ1,subQ0]});Q4=makeQuery(id+"F13.boolean.opBoolean","COPY",EDGE,{"derivedFrom":makeQuery(id+"F13.opExtrude","TWEAK_EDGE",EDGE,{"derivedFrom":[makeQuery(id+"F12.imprint","IMPRINT",EDGE,{"disambiguationData":[TD([[subQ2,-1.0]])],"derivedFrom":subQ1}),makeQuery(id+"F12.imprint","IMPRINT",EDGE,{"disambiguationData":[TD([[makeQuery(id+"F12.imprint","INTERSECT",VERTEX,{"derivedFrom":[subQ1,sQuery(id+"F12.wireOp",EDGE,"E50.right")]}),1.0]])],"derivedFrom":subQ1}),makeQuery(id+"F12.imprint","IMPRINT",EDGE,{"disambiguationData":[TD([[makeQuery(id+"F12.imprint","INTERSECT",VERTEX,{"derivedFrom":[sQuery(id+"F12.wireOp",EDGE,"E50.bottom"),subQ0]}),-1.0]])],"derivedFrom":subQ0}),makeQuery(id+"F12.imprint","IMPRINT",EDGE,{"disambiguationData":[TD([[subQ2,1.0]])],"derivedFrom":subQ0})]})});}
            var Q5;
            {var subQ0=sQuery(id+"F12.wireOp",EDGE,"E50.right");var subQ1=sQuery(id+"F12.wireOp",EDGE,"E50.top");var subQ2=makeQuery(id+"F12.imprint","INTERSECT",VERTEX,{"derivedFrom":[subQ1,subQ0]});Q5=makeQuery(id+"F13.boolean.opBoolean","COPY",EDGE,{"derivedFrom":makeQuery(id+"F13.opExtrude","TWEAK_EDGE",EDGE,{"derivedFrom":[makeQuery(id+"F12.imprint","IMPRINT",EDGE,{"disambiguationData":[TD([[makeQuery(id+"F12.imprint","INTERSECT",VERTEX,{"derivedFrom":[subQ1,sQuery(id+"F12.wireOp",EDGE,"E50.left")]}),-1.0]])],"derivedFrom":subQ1}),makeQuery(id+"F12.imprint","IMPRINT",EDGE,{"disambiguationData":[TD([[subQ2,1.0]])],"derivedFrom":subQ1}),makeQuery(id+"F12.imprint","IMPRINT",EDGE,{"disambiguationData":[TD([[makeQuery(id+"F12.imprint","INTERSECT",VERTEX,{"derivedFrom":[sQuery(id+"F12.wireOp",EDGE,"E50.bottom"),subQ0]}),-1.0]])],"derivedFrom":subQ0}),makeQuery(id+"F12.imprint","IMPRINT",EDGE,{"disambiguationData":[TD([[subQ2,1.0]])],"derivedFrom":subQ0})]})});}
            var Q6;
            Q6=makeQuery(id+"F6.boolean.opBoolean","COPY",EDGE,{"derivedFrom":makeQuery(id+"F6.opRevolve","SWEPT_EDGE",EDGE,{"disambiguationData":[OSD([sQuery(id+"F5.wireOp",EDGE,"E15"),sQuery(id+"F5.wireOp",EDGE,"E16")])]})});
            fillet(context, id + "F25", {"entities" : qUnion([Q0, Q1, Q2, Q3, Q4, Q5, Q6]), "radius" : 2 * mm, "tangentPropagation" : true, "allowEdgeOverflow" : false});
        }
    });
